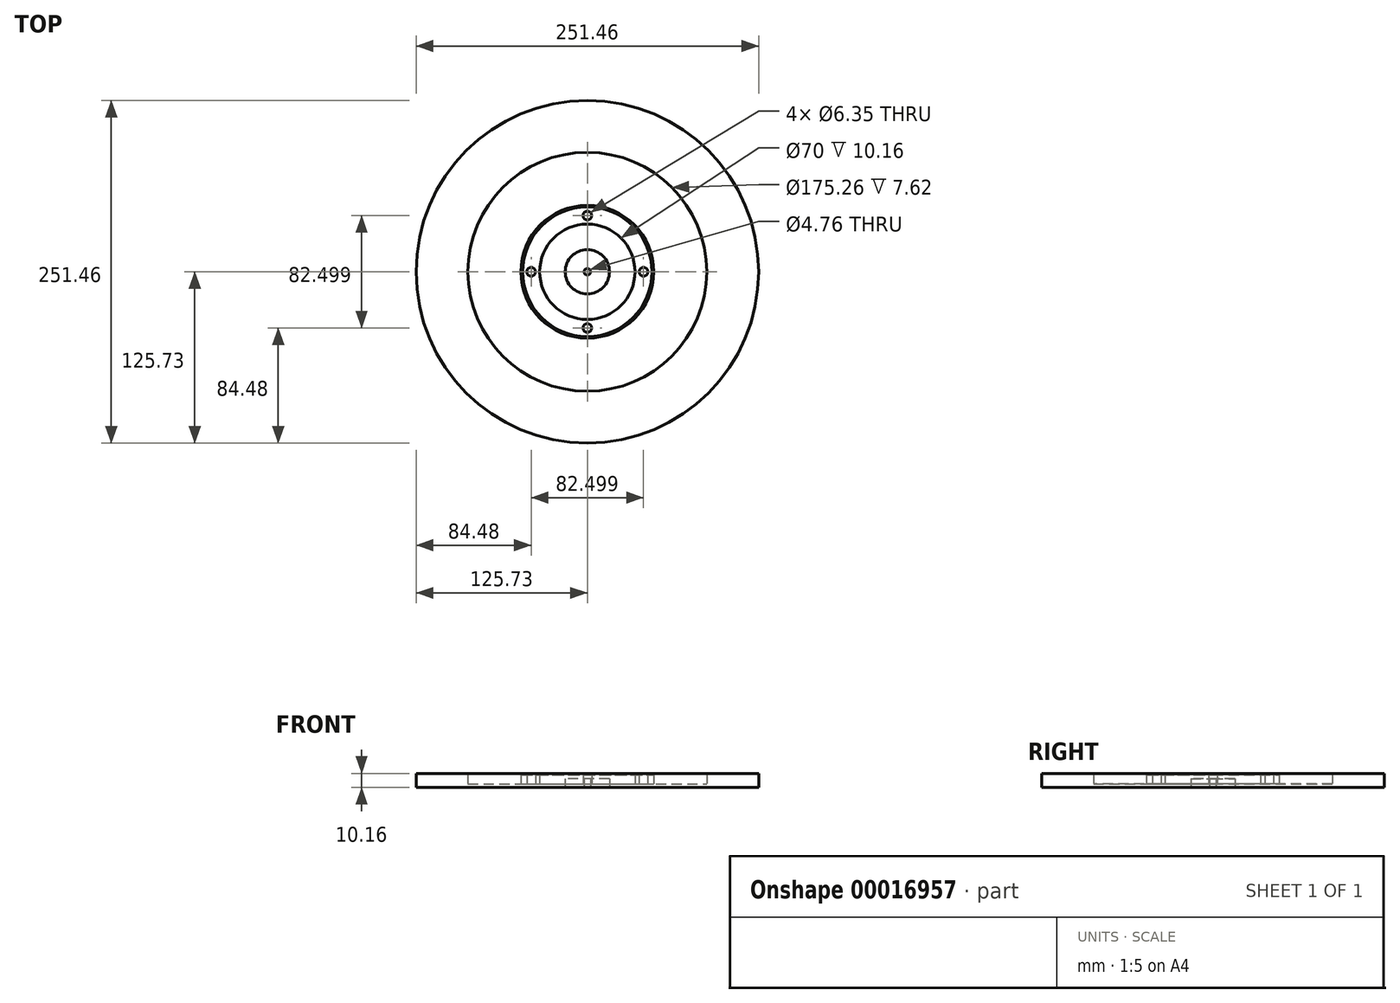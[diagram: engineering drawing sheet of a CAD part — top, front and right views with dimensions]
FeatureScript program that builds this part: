
annotation { "Feature Type Name" : "Feature", "Feature Type Description" : "" }
export const myFeature = defineFeature(function(context is Context, id is Id, definition is map)
    precondition{}
    {
        {
            var Q0;
            Q0=qCreatedBy(makeId("Top.planeOp"),FACE);
            var sketch = newSketch(context, id + "F0", { "sketchPlane" : qUnion([Q0])});
            skCircle(sketch, "E0", {"center": v(0, 0) * mm, "radius": 48.77 * mm});
            skCircle(sketch, "E1", {"center": v(0, 0) * mm, "radius": 38.5 * mm});
            skCircle(sketch, "E2", {"center": v(0, 0) * mm, "radius": 16.26 * mm});
            skCircle(sketch, "E3", {"center": v(0, 0) * mm, "radius": 2.38 * mm});
            skLineSegment(sketch, "E4", {"start": v(0, 0) * mm, "end": v(0, 48.77) * mm, "construction": true});
            skCircle(sketch, "E5", {"center": v(0, 0) * mm, "radius": 41.25 * mm, "construction": true});
            skPoint(sketch, "E6", {"position": v(0, 41.25) * mm});
            skPoint(sketch, "E7.1.0", {"position": v(-41.25, 0) * mm});
            skPoint(sketch, "E7.2.0", {"position": v(0, -41.25) * mm});
            skPoint(sketch, "E7.3.0", {"position": v(41.25, 0) * mm});
            skSolve(sketch);
        }
        {
            var Q0;
            Q0=makeQuery(id+"F0.imprint","IMPRINT",FACE,{"disambiguationData":[TD([[makeQuery(id+"F0.imprint","IMPRINT",EDGE,{"derivedFrom":sQuery(id+"F0.wireOp",EDGE,"E2")}),1.0]])]});
            extrude(context, id + "F1", {"entities" : qUnion([Q0]), "depth" : 6.35 * mm});
        }
        {
            var Q0;
            Q0=qCreatedBy(makeId("Right.planeOp"),FACE);
            var sketch = newSketch(context, id + "F2", { "sketchPlane" : qUnion([Q0])});
            skLineSegment(sketch, "E8", {"start": v(0, 0) * mm, "end": v(-63.36, 0) * mm, "construction": true});
            skLineSegment(sketch, "E9", {"start": v(-35, 0) * mm, "end": v(-35, 10.16) * mm});
            skLineSegment(sketch, "E10", {"start": v(-35, 10.16) * mm, "end": v(-47.5, 10.16) * mm});
            skLineSegment(sketch, "E11", {"start": v(-47.5, 10.16) * mm, "end": v(-47.5, 9.14) * mm});
            skLineSegment(sketch, "E12", {"start": v(-47.5, 9.14) * mm, "end": v(-48.77, 9.14) * mm});
            skLineSegment(sketch, "E13", {"start": v(-48.77, 9.14) * mm, "end": v(-48.77, 2.54) * mm});
            skLineSegment(sketch, "E14", {"start": v(-48.77, 2.54) * mm, "end": v(-87.63, 2.54) * mm});
            skLineSegment(sketch, "E15", {"start": v(-87.63, 2.54) * mm, "end": v(-87.63, 10.16) * mm});
            skLineSegment(sketch, "E16", {"start": v(-87.63, 10.16) * mm, "end": v(-125.73, 10.16) * mm});
            skLineSegment(sketch, "E17", {"start": v(-125.73, 10.16) * mm, "end": v(-125.73, 0) * mm});
            skLineSegment(sketch, "E18", {"start": v(-125.73, 0) * mm, "end": v(-35, 0) * mm});
            skSolve(sketch);
        }
        {
            var Q0;
            Q0=makeQuery(id+"F2.imprint","IMPRINT",FACE,{"disambiguationData":[TD([[makeQuery(id+"F2.imprint","IMPRINT",EDGE,{"derivedFrom":sQuery(id+"F2.wireOp",EDGE,"E9")}),1.0]])]});
            var Q1;
            Q1=sQuery(id+"F0.wireOp",EDGE,"E3");
            revolve(context, id + "F3", {"entities" : qUnion([Q0]), "axis" : qUnion([Q1]), "revolveType" : RevolveType.FULL});
        }
        {
            var Q0;
            Q0=sQuery(id+"F0.wireOp",VERTEX,"E7.3.0");
            var Q1;
            Q1=sQuery(id+"F0.wireOp",VERTEX,"E6");
            var Q2;
            Q2=sQuery(id+"F0.wireOp",VERTEX,"E7.1.0");
            var Q3;
            Q3=sQuery(id+"F0.wireOp",VERTEX,"E7.2.0");
            var Q4;
            Q4=makeQuery(id+"F3.opRevolve","SWEPT_BODY",BODY,{"disambiguationData":[OSD([sQuery(id+"F2.wireOp",EDGE,"E9"),sQuery(id+"F2.wireOp",EDGE,"E10"),sQuery(id+"F2.wireOp",EDGE,"E11"),sQuery(id+"F2.wireOp",EDGE,"E12"),sQuery(id+"F2.wireOp",EDGE,"E13"),sQuery(id+"F2.wireOp",EDGE,"E14"),sQuery(id+"F2.wireOp",EDGE,"E15"),sQuery(id+"F2.wireOp",EDGE,"E16"),sQuery(id+"F2.wireOp",EDGE,"E17"),sQuery(id+"F2.wireOp",EDGE,"E18")])]});
            hole(context, id + "F4", {"style" : HoleStyle.SIMPLE, "holeDiameter" : 6.35 * mm, "endStyle" : HoleEndStyle.THROUGH, "oppositeDirection" : true, "locations" : qUnion([Q0, Q1, Q2, Q3]), "scope" : qUnion([Q4])});
        }
    });
